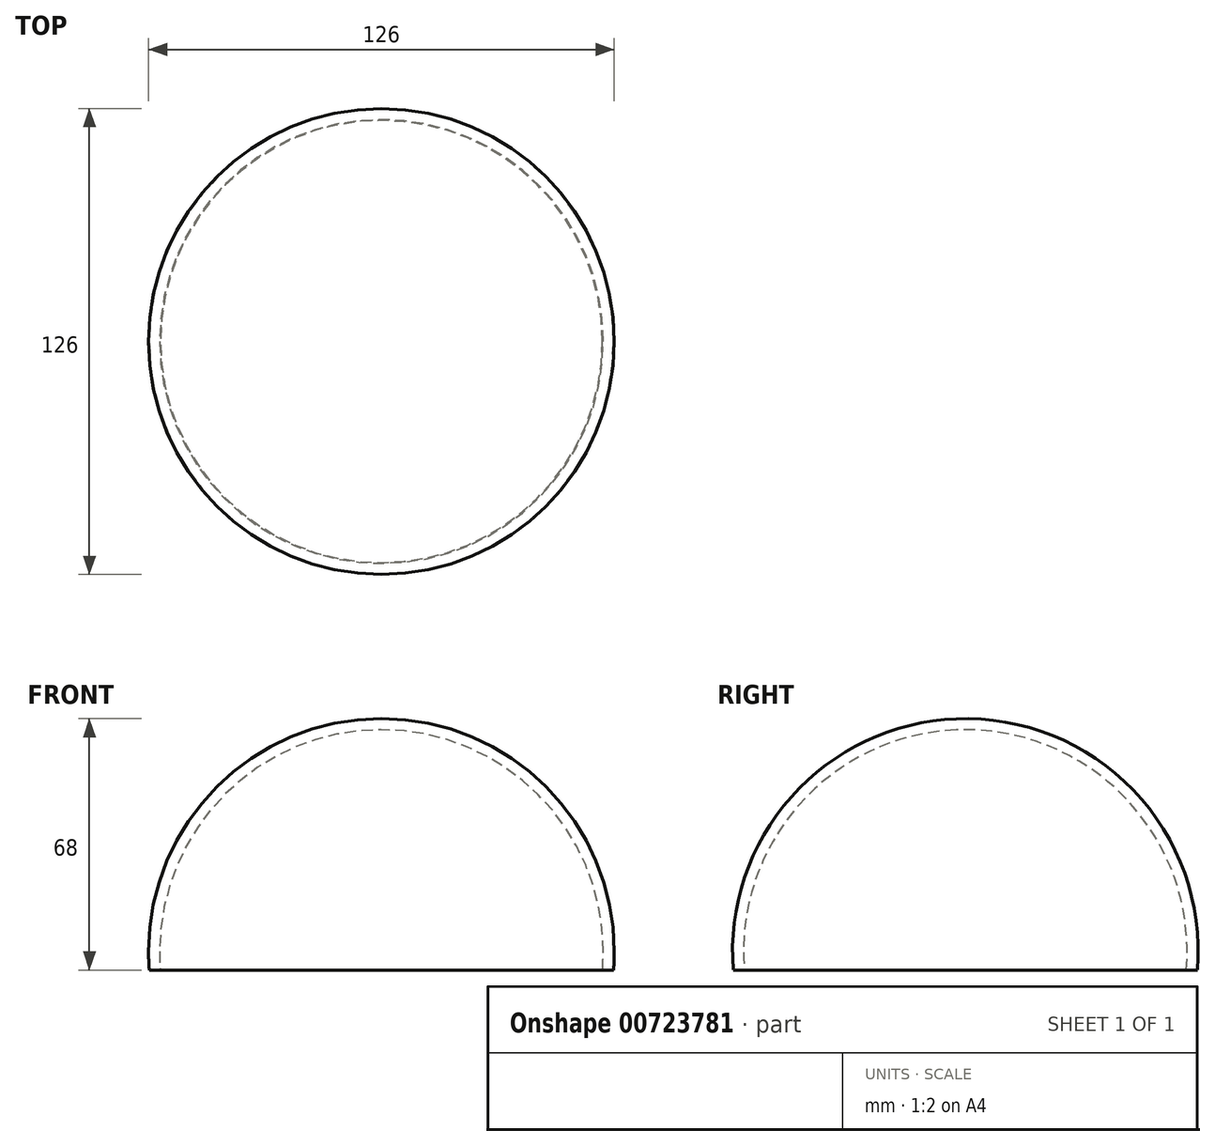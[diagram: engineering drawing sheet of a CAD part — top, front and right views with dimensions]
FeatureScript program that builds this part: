
annotation { "Feature Type Name" : "Feature", "Feature Type Description" : "" }
export const myFeature = defineFeature(function(context is Context, id is Id, definition is map)
    precondition{}
    {
        {
            var Q0;
            Q0=qCreatedBy(makeId("Top.planeOp"),FACE);
            var sketch = newSketch(context, id + "F0", { "sketchPlane" : qUnion([Q0])});
            skArc(sketch, "E0", {"start": v(-63, 0) * mm, "mid": v(0, -63) * mm, "end": v(63, 0) * mm});
            skArc(sketch, "E1.0", {"start": v(-60, 0) * mm, "mid": v(0, -60) * mm, "end": v(60, 0) * mm});
            skLineSegment(sketch, "E2", {"start": v(60, 0) * mm, "end": v(63, 0) * mm});
            skLineSegment(sketch, "E3", {"start": v(-60, 0) * mm, "end": v(-63, 0) * mm});
            skLineSegment(sketch, "E4", {"start": v(60, 0) * mm, "end": v(-60, 0) * mm, "construction": true});
            skSolve(sketch);
        }
        {
            var Q0;
            Q0=makeQuery(id+"F0.imprint","IMPRINT",FACE,{"disambiguationData":[TD([[makeQuery(id+"F0.imprint","IMPRINT",EDGE,{"derivedFrom":sQuery(id+"F0.wireOp",EDGE,"E0")}),1.0]])]});
            var Q1;
            Q1=sQuery(id+"F0.wireOp",EDGE,"E4");
            revolve(context, id + "F1", {"entities" : qUnion([Q0]), "axis" : qUnion([Q1]), "revolveType" : RevolveType.ONE_DIRECTION, "angle" : 360 * degree});
        }
        {
            var Q0;
            Q0=qCreatedBy(makeId("Right.planeOp"),FACE);
            var sketch = newSketch(context, id + "F2", { "sketchPlane" : qUnion([Q0])});
            skLineSegment(sketch, "E5", {"start": v(75, 0) * mm, "end": v(75, -5) * mm});
            skLineSegment(sketch, "E6", {"start": v(75, -5) * mm, "end": v(-75, -5) * mm});
            skLineSegment(sketch, "E7", {"start": v(-75, -5) * mm, "end": v(-75, -65) * mm});
            skLineSegment(sketch, "E8", {"start": v(-75, -65) * mm, "end": v(75, -65) * mm});
            skLineSegment(sketch, "E9", {"start": v(75, -65) * mm, "end": v(75, -5) * mm});
            skSolve(sketch);
        }
        {
            var Q0;
            Q0=makeQuery(id+"F2.imprint","IMPRINT",FACE,{"disambiguationData":[TD([[makeQuery(id+"F2.imprint","IMPRINT",EDGE,{"derivedFrom":sQuery(id+"F2.wireOp",EDGE,"E6")}),1.0]])]});
            extrude(context, id + "F3", {"entities" : qUnion([Q0]), "operationType" : NewBodyOperationType.REMOVE, "oppositeDirection" : true, "depth" : 126 * mm, "symmetric" : true});
        }
    });
